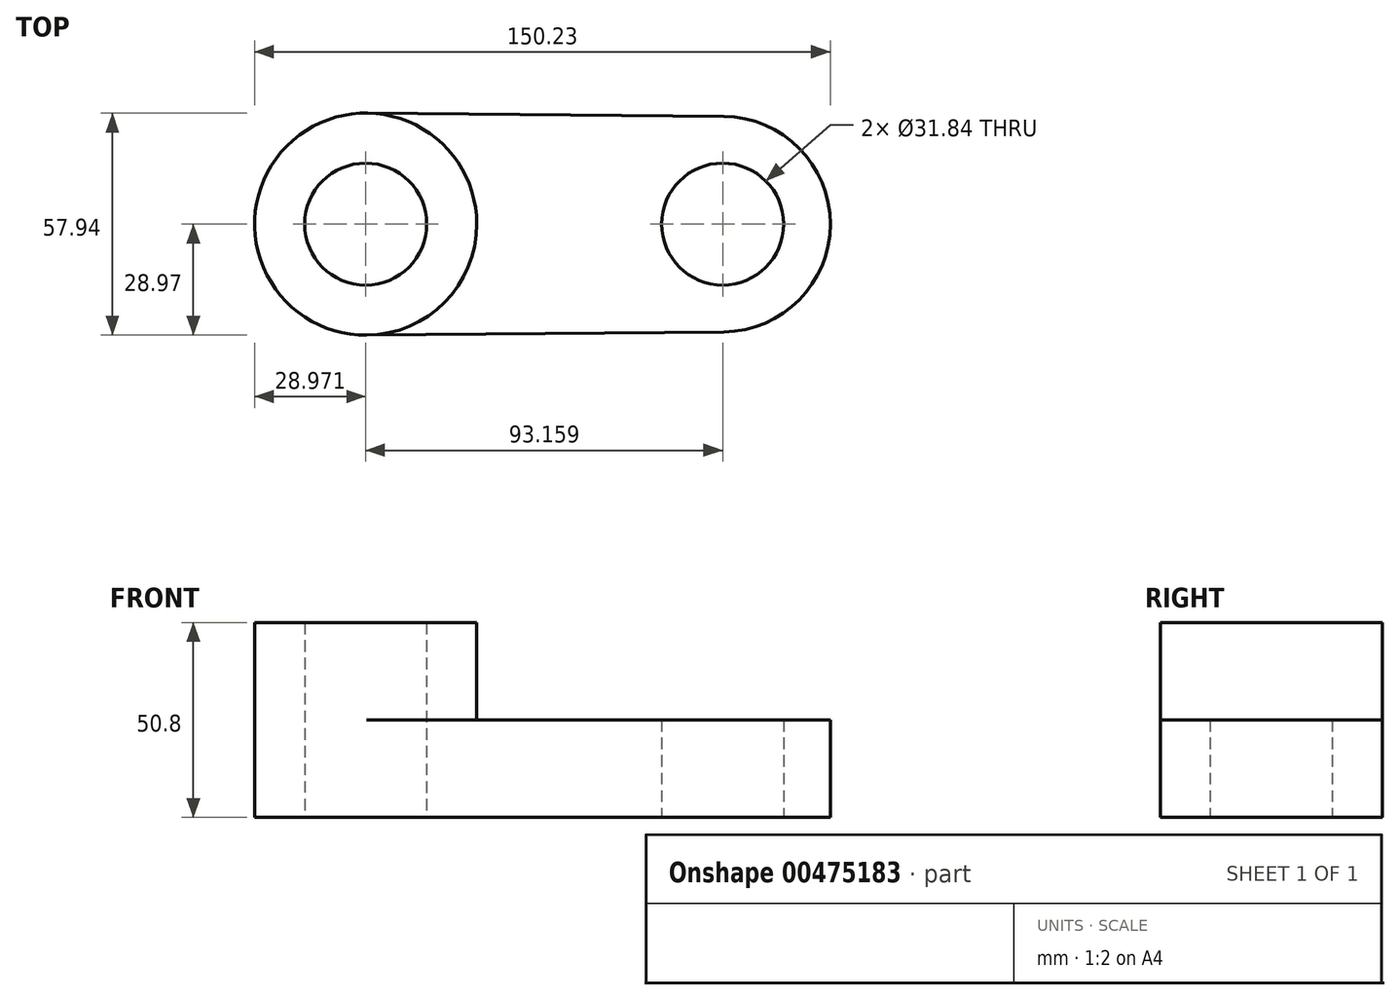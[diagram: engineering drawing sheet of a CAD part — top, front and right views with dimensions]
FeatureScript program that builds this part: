
annotation { "Feature Type Name" : "Feature", "Feature Type Description" : "" }
export const myFeature = defineFeature(function(context is Context, id is Id, definition is map)
    precondition{}
    {
        {
            var Q0;
            Q0=qCreatedBy(makeId("Top.planeOp"),FACE);
            var sketch = newSketch(context, id + "F0", { "sketchPlane" : qUnion([Q0])});
            skCircle(sketch, "E0", {"center": v(-46.58, 0) * mm, "radius": 15.92 * mm});
            skCircle(sketch, "E1", {"center": v(46.58, 0) * mm, "radius": 15.92 * mm});
            skArc(sketch, "E2", {"start": v(-46.3, 28.97) * mm, "mid": v(-75.55, 0) * mm, "end": v(-46.3, -28.97) * mm});
            skArc(sketch, "E3", {"start": v(46.84, -28.1) * mm, "mid": v(74.68, 0) * mm, "end": v(46.84, 28.1) * mm});
            skLineSegment(sketch, "E4", {"start": v(-46.3, 28.97) * mm, "end": v(46.84, 28.1) * mm});
            skLineSegment(sketch, "E5", {"start": v(46.84, -28.1) * mm, "end": v(-46.3, -28.97) * mm});
            skArc(sketch, "E6", {"start": v(-46.3, -28.97) * mm, "mid": v(-17.6, 0) * mm, "end": v(-46.3, 28.97) * mm});
            skSolve(sketch);
        }
        {
            var Q0;
            Q0=makeQuery(id+"F0.imprint","IMPRINT",FACE,{"disambiguationData":[TD([[makeQuery(id+"F0.imprint","IMPRINT",EDGE,{"derivedFrom":sQuery(id+"F0.wireOp",EDGE,"E0")}),-1.0]])]});
            extrude(context, id + "F1", {"entities" : qUnion([Q0]), "depth" : 25.4 * mm});
        }
        {
            var Q0;
            Q0=makeQuery(id+"F0.imprint","IMPRINT",FACE,{"disambiguationData":[TD([[makeQuery(id+"F0.imprint","IMPRINT",EDGE,{"derivedFrom":sQuery(id+"F0.wireOp",EDGE,"E1")}),-1.0]])]});
            extrude(context, id + "F2", {"entities" : qUnion([Q0]), "operationType" : NewBodyOperationType.ADD, "depth" : 25.4 * mm});
        }
        {
            var Q0;
            Q0=makeQuery(id+"F0.imprint","IMPRINT",FACE,{"disambiguationData":[TD([[makeQuery(id+"F0.imprint","IMPRINT",EDGE,{"derivedFrom":sQuery(id+"F0.wireOp",EDGE,"E0")}),-1.0]])]});
            extrude(context, id + "F3", {"entities" : qUnion([Q0]), "operationType" : NewBodyOperationType.ADD, "depth" : 50.8 * mm});
        }
    });
